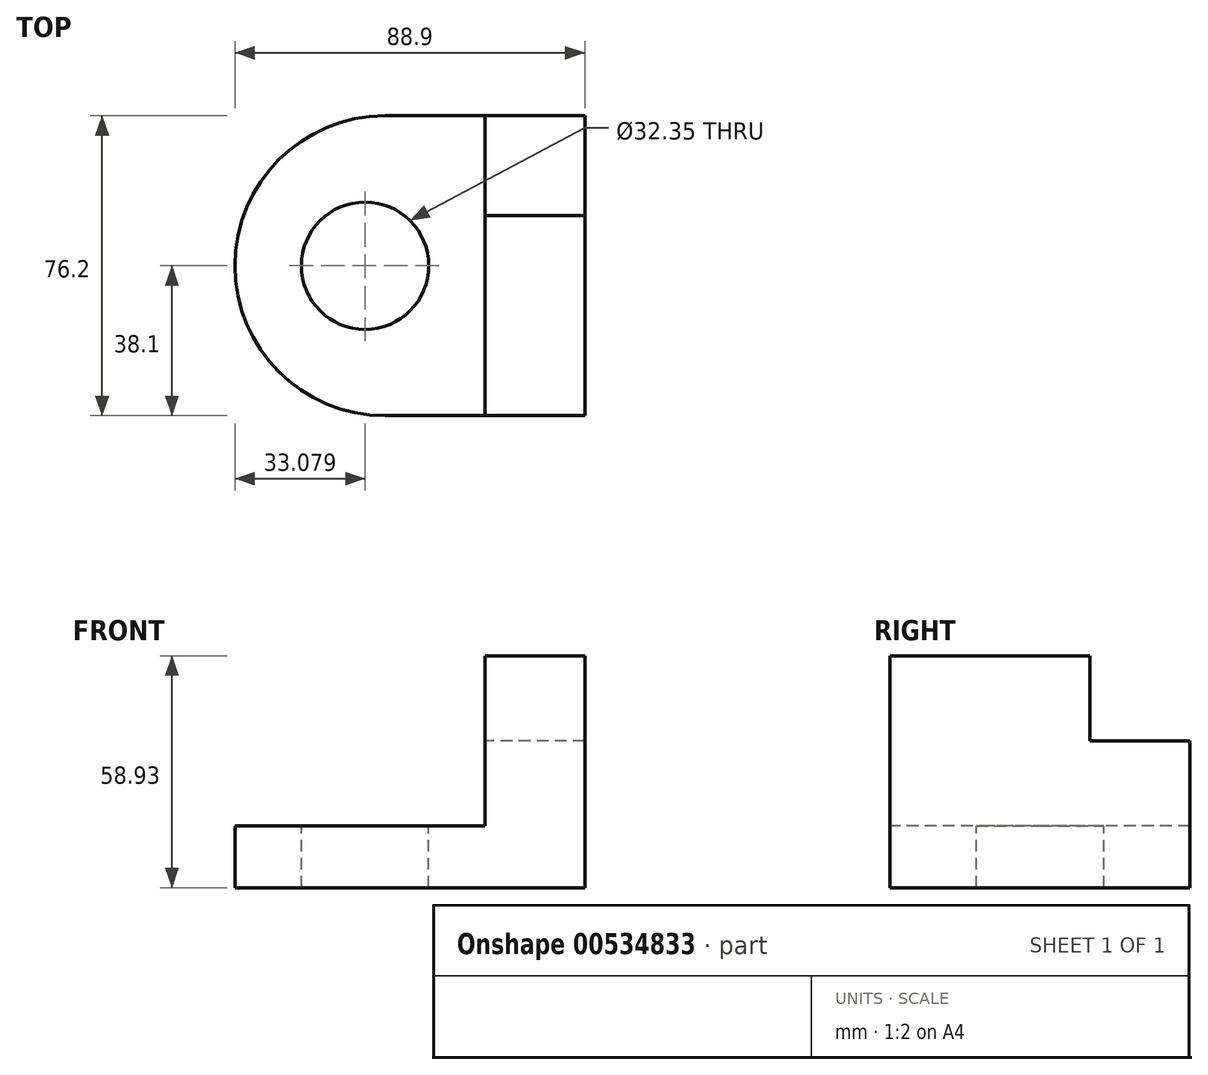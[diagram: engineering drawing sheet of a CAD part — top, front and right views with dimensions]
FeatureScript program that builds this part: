
annotation { "Feature Type Name" : "Feature", "Feature Type Description" : "" }
export const myFeature = defineFeature(function(context is Context, id is Id, definition is map)
    precondition{}
    {
        {
            var Q0;
            Q0=qCreatedBy(makeId("Top.planeOp"),FACE);
            var sketch = newSketch(context, id + "F0", { "sketchPlane" : qUnion([Q0])});
            skLineSegment(sketch, "E0.bottom", {"start": v(25.4, 38.1) * mm, "end": v(-25.4, 38.1) * mm});
            skLineSegment(sketch, "E0.top", {"start": v(25.4, -38.1) * mm, "end": v(-25.4, -38.1) * mm});
            skLineSegment(sketch, "E0.left", {"start": v(25.4, 38.1) * mm, "end": v(25.4, -38.1) * mm});
            skLineSegment(sketch, "E0.right", {"start": v(-25.4, 38.1) * mm, "end": v(-25.4, -38.1) * mm});
            skPoint(sketch, "E0.middle", {"position": v(0, 0) * mm});
            skArc(sketch, "E1", {"start": v(-25.4, 38.1) * mm, "mid": v(-63.5, 0) * mm, "end": v(-25.4, -38.1) * mm});
            skSolve(sketch);
        }
        {
            var Q0;
            Q0=makeQuery(id+"F0.imprint","IMPRINT",FACE,{"disambiguationData":[TD([[makeQuery(id+"F0.imprint","IMPRINT",EDGE,{"derivedFrom":sQuery(id+"F0.wireOp",EDGE,"E0.bottom")}),1.0]])]});
            var Q1;
            Q1=makeQuery(id+"F0.imprint","IMPRINT",FACE,{"disambiguationData":[TD([[makeQuery(id+"F0.imprint","IMPRINT",EDGE,{"derivedFrom":sQuery(id+"F0.wireOp",EDGE,"E0.right")}),-1.0]])]});
            extrude(context, id + "F1", {"entities" : qUnion([Q0, Q1]), "depth" : 15.75 * mm, "offsetDistance" : 25.4 * mm});
        }
        {
            var Q0;
            Q0=makeQuery(id+"F1.opExtrude","CAP_FACE",FACE,{"disambiguationData":[OSD([sQuery(id+"F0.wireOp",EDGE,"E0.bottom"),sQuery(id+"F0.wireOp",EDGE,"E0.top"),sQuery(id+"F0.wireOp",EDGE,"E0.left"),sQuery(id+"F0.wireOp",EDGE,"E1")])],"isStart":false});
            var sketch = newSketch(context, id + "F2", { "sketchPlane" : qUnion([Q0])});
            skCircle(sketch, "E2", {"center": v(-30.42, 0) * mm, "radius": 16.17 * mm});
            skSolve(sketch);
        }
        {
            var Q0;
            Q0=makeQuery(id+"F2.imprint","IMPRINT",FACE,{"disambiguationData":[TD([[makeQuery(id+"F2.imprint","IMPRINT",EDGE,{"derivedFrom":sQuery(id+"F2.wireOp",EDGE,"E2")}),1.0]])]});
            extrude(context, id + "F3", {"entities" : qUnion([Q0]), "operationType" : NewBodyOperationType.REMOVE, "oppositeDirection" : true, "depth" : 25.4 * mm, "offsetDistance" : 25.4 * mm});
        }
        {
            var Q0;
            Q0=makeQuery(id+"F1.opExtrude","CAP_FACE",FACE,{"disambiguationData":[OSD([sQuery(id+"F0.wireOp",EDGE,"E0.bottom"),sQuery(id+"F0.wireOp",EDGE,"E0.top"),sQuery(id+"F0.wireOp",EDGE,"E0.left"),sQuery(id+"F0.wireOp",EDGE,"E1")])],"isStart":false});
            var sketch = newSketch(context, id + "F4", { "sketchPlane" : qUnion([Q0])});
            skLineSegment(sketch, "E3.bottom", {"start": v(25.4, 38.1) * mm, "end": v(0, 38.1) * mm});
            skLineSegment(sketch, "E3.top", {"start": v(25.4, -38.1) * mm, "end": v(0, -38.1) * mm});
            skLineSegment(sketch, "E3.left", {"start": v(25.4, 38.1) * mm, "end": v(25.4, -38.1) * mm});
            skLineSegment(sketch, "E3.right", {"start": v(0, 38.1) * mm, "end": v(0, -38.1) * mm});
            skSolve(sketch);
        }
        {
            var Q0;
            Q0=makeQuery(id+"F4.imprint","IMPRINT",FACE,{"disambiguationData":[TD([[makeQuery(id+"F4.imprint","IMPRINT",EDGE,{"derivedFrom":sQuery(id+"F4.wireOp",EDGE,"E3.bottom")}),1.0]])]});
            extrude(context, id + "F5", {"entities" : qUnion([Q0]), "operationType" : NewBodyOperationType.ADD, "depth" : 43.18 * mm, "offsetDistance" : 25.4 * mm});
        }
        {
            var Q0;
            Q0=makeQuery(id+"F5.opExtrude","CAP_FACE",FACE,{"disambiguationData":[OSD([sQuery(id+"F4.wireOp",EDGE,"E3.bottom"),sQuery(id+"F4.wireOp",EDGE,"E3.top"),sQuery(id+"F4.wireOp",EDGE,"E3.left"),sQuery(id+"F4.wireOp",EDGE,"E3.right")])],"isStart":false});
            var sketch = newSketch(context, id + "F6", { "sketchPlane" : qUnion([Q0])});
            skLineSegment(sketch, "E4.bottom", {"start": v(25.4, 38.1) * mm, "end": v(0, 38.1) * mm});
            skLineSegment(sketch, "E4.top", {"start": v(25.4, 12.7) * mm, "end": v(0, 12.7) * mm});
            skLineSegment(sketch, "E4.left", {"start": v(25.4, 38.1) * mm, "end": v(25.4, 12.7) * mm});
            skLineSegment(sketch, "E4.right", {"start": v(0, 38.1) * mm, "end": v(0, 12.7) * mm});
            skSolve(sketch);
        }
        {
            var Q0;
            Q0=makeQuery(id+"F6.imprint","IMPRINT",FACE,{"disambiguationData":[TD([[makeQuery(id+"F6.imprint","IMPRINT",EDGE,{"derivedFrom":sQuery(id+"F6.wireOp",EDGE,"E4.bottom")}),1.0]])]});
            extrude(context, id + "F7", {"entities" : qUnion([Q0]), "operationType" : NewBodyOperationType.REMOVE, "oppositeDirection" : true, "depth" : 21.59 * mm, "offsetDistance" : 25.4 * mm});
        }
    });
